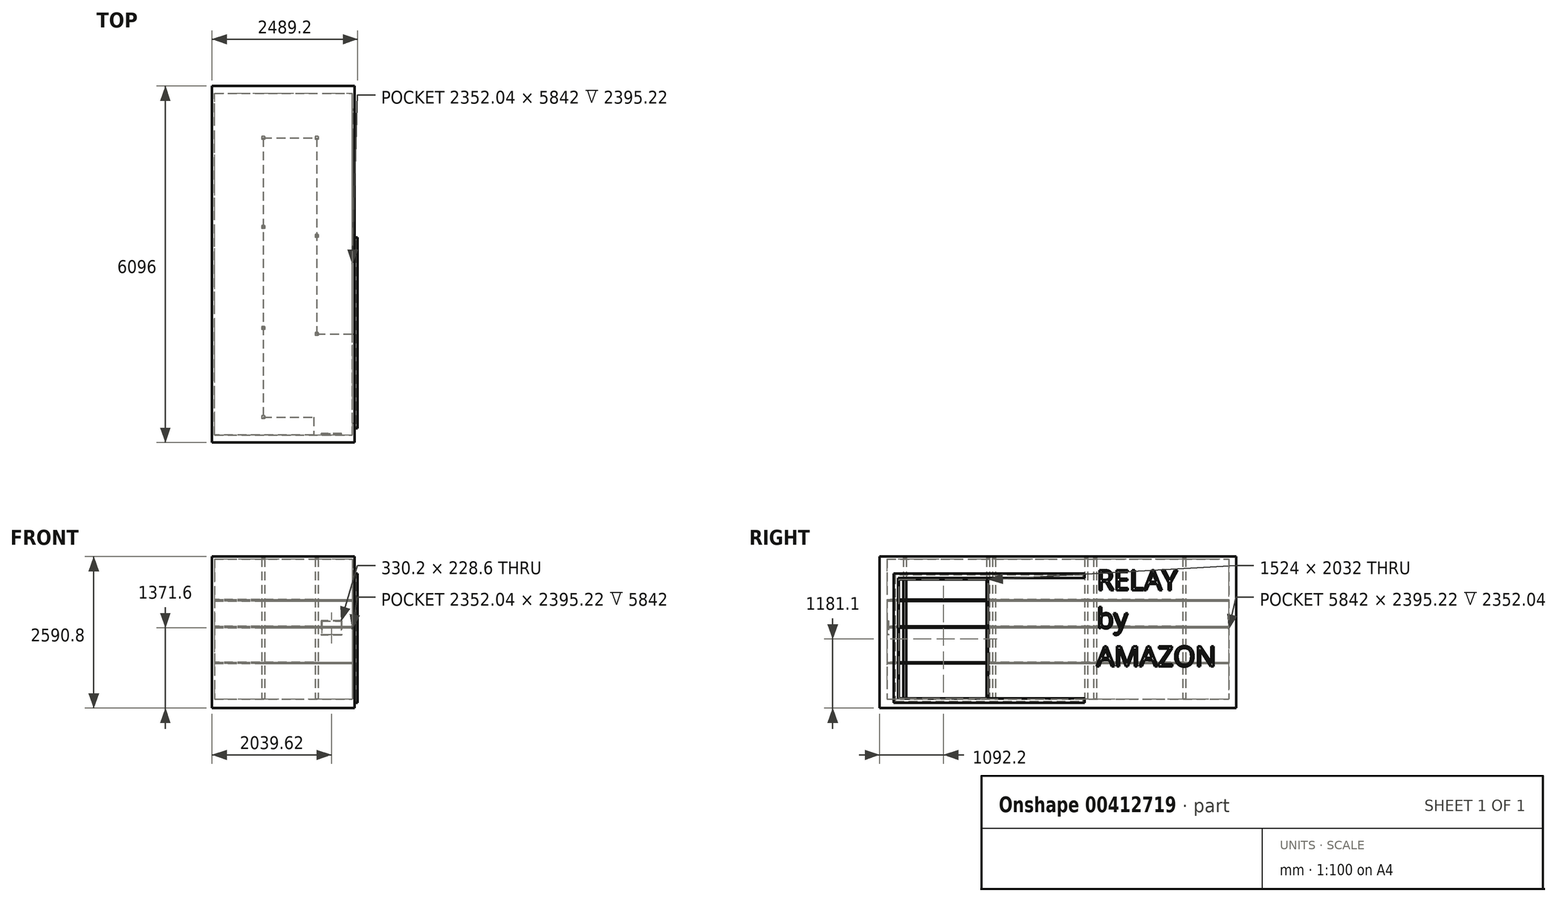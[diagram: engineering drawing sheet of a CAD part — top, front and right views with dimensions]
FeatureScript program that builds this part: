
annotation { "Feature Type Name" : "Feature", "Feature Type Description" : "" }
export const myFeature = defineFeature(function(context is Context, id is Id, definition is map)
    precondition{}
    {
        {
            var Q0;
            Q0=qCreatedBy(makeId("Front.planeOp"),FACE);
            var sketch = newSketch(context, id + "F0", { "sketchPlane" : qUnion([Q0])});
            skLineSegment(sketch, "E0.bottom", {"start": v(-1219.2, 1295.4) * mm, "end": v(1219.2, 1295.4) * mm});
            skLineSegment(sketch, "E0.top", {"start": v(-1219.2, -1295.4) * mm, "end": v(1219.2, -1295.4) * mm});
            skLineSegment(sketch, "E0.left", {"start": v(-1219.2, 1295.4) * mm, "end": v(-1219.2, -1295.4) * mm});
            skLineSegment(sketch, "E0.right", {"start": v(1219.2, 1295.4) * mm, "end": v(1219.2, -1295.4) * mm});
            skPoint(sketch, "E1", {"position": v(0, 1295.4) * mm});
            skPoint(sketch, "E2", {"position": v(-1219.2, 0) * mm});
            skLineSegment(sketch, "E3.bottom", {"start": v(-1176.02, 1252.22) * mm, "end": v(1176.02, 1252.22) * mm});
            skLineSegment(sketch, "E3.top", {"start": v(-1176.02, -1143) * mm, "end": v(1176.02, -1143) * mm});
            skLineSegment(sketch, "E3.left", {"start": v(-1176.02, 1252.22) * mm, "end": v(-1176.02, -1143) * mm});
            skLineSegment(sketch, "E3.right", {"start": v(1176.02, 1252.22) * mm, "end": v(1176.02, -1143) * mm});
            skPoint(sketch, "E4", {"position": v(0, 1252.22) * mm});
            skSolve(sketch);
        }
        {
            var Q0;
            Q0=makeQuery(id+"F0.imprint","IMPRINT",FACE,{"disambiguationData":[TD([[makeQuery(id+"F0.imprint","IMPRINT",EDGE,{"derivedFrom":sQuery(id+"F0.wireOp",EDGE,"E0.bottom")}),-1.0]])]});
            extrude(context, id + "F1", {"entities" : qUnion([Q0]), "depth" : 6096 * mm});
        }
        {
            var Q0;
            Q0=makeQuery(id+"F1.opExtrude","CAP_FACE",FACE,{"disambiguationData":[OSD([sQuery(id+"F0.wireOp",EDGE,"E0.bottom"),sQuery(id+"F0.wireOp",EDGE,"E0.top"),sQuery(id+"F0.wireOp",EDGE,"E0.left"),sQuery(id+"F0.wireOp",EDGE,"E0.right"),sQuery(id+"F0.wireOp",EDGE,"E3.bottom"),sQuery(id+"F0.wireOp",EDGE,"E3.top"),sQuery(id+"F0.wireOp",EDGE,"E3.left"),sQuery(id+"F0.wireOp",EDGE,"E3.right")])],"isStart":true});
            var sketch = newSketch(context, id + "F2", { "sketchPlane" : qUnion([Q0])});
            skLineSegment(sketch, "E5.0", {"start": v(1176.02, -1143) * mm, "end": v(-1176.02, -1143) * mm});
            skLineSegment(sketch, "E5.1", {"start": v(-1176.02, 1252.22) * mm, "end": v(-1176.02, -1143) * mm});
            skLineSegment(sketch, "E5.2", {"start": v(1176.02, 1252.22) * mm, "end": v(-1176.02, 1252.22) * mm});
            skLineSegment(sketch, "E5.3", {"start": v(1176.02, 1252.22) * mm, "end": v(1176.02, -1143) * mm});
            skSolve(sketch);
        }
        {
            var Q0;
            Q0 = qSketchRegion(id + "F2", true);
            extrude(context, id + "F3", {"entities" : qUnion([Q0]), "operationType" : NewBodyOperationType.ADD, "oppositeDirection" : true, "depth" : 127 * mm});
        }
        {
            var Q0;
            Q0=makeQuery(id+"F1.opExtrude","CAP_FACE",FACE,{"disambiguationData":[OSD([sQuery(id+"F0.wireOp",EDGE,"E0.bottom"),sQuery(id+"F0.wireOp",EDGE,"E0.top"),sQuery(id+"F0.wireOp",EDGE,"E0.left"),sQuery(id+"F0.wireOp",EDGE,"E0.right"),sQuery(id+"F0.wireOp",EDGE,"E3.bottom"),sQuery(id+"F0.wireOp",EDGE,"E3.top"),sQuery(id+"F0.wireOp",EDGE,"E3.left"),sQuery(id+"F0.wireOp",EDGE,"E3.right")])],"isStart":false});
            var sketch = newSketch(context, id + "F4", { "sketchPlane" : qUnion([Q0])});
            skLineSegment(sketch, "E6.0", {"start": v(-1176.02, -1143) * mm, "end": v(1176.02, -1143) * mm});
            skLineSegment(sketch, "E6.1", {"start": v(1176.02, 1252.22) * mm, "end": v(1176.02, -1143) * mm});
            skLineSegment(sketch, "E6.2", {"start": v(-1176.02, 1252.22) * mm, "end": v(1176.02, 1252.22) * mm});
            skLineSegment(sketch, "E6.3", {"start": v(-1176.02, 1252.22) * mm, "end": v(-1176.02, -1143) * mm});
            skSolve(sketch);
        }
        {
            var Q0;
            Q0 = qSketchRegion(id + "F4", true);
            extrude(context, id + "F5", {"entities" : qUnion([Q0]), "operationType" : NewBodyOperationType.ADD, "oppositeDirection" : true, "depth" : 127 * mm});
        }
        {
            var Q0;
            Q0=makeQuery(id+"F1.opExtrude","SWEPT_FACE",FACE,{"disambiguationData":[OSD([sQuery(id+"F0.wireOp",EDGE,"E0.right")])]});
            var sketch = newSketch(context, id + "F6", { "sketchPlane" : qUnion([Q0])});
            skLineSegment(sketch, "E7.bottom", {"start": v(-5765.8, 901.7) * mm, "end": v(-4241.8, 901.7) * mm});
            skLineSegment(sketch, "E7.top", {"start": v(-5765.8, -1130.3) * mm, "end": v(-4241.8, -1130.3) * mm});
            skLineSegment(sketch, "E7.left", {"start": v(-5765.8, 901.7) * mm, "end": v(-5765.8, -1130.3) * mm});
            skLineSegment(sketch, "E7.right", {"start": v(-4241.8, 901.7) * mm, "end": v(-4241.8, -1130.3) * mm});
            skSolve(sketch);
        }
        {
            var Q0;
            Q0 = qSketchRegion(id + "F6", true);
            extrude(context, id + "F7", {"entities" : qUnion([Q0]), "operationType" : NewBodyOperationType.REMOVE, "oppositeDirection" : true, "depth" : 50.8 * mm});
        }
        {
            var Q0;
            Q0=makeQuery(id+"F1.opExtrude","SWEPT_FACE",FACE,{"disambiguationData":[OSD([sQuery(id+"F0.wireOp",EDGE,"E0.right")])]});
            var sketch = newSketch(context, id + "F8", { "sketchPlane" : qUnion([Q0])});
            skLineSegment(sketch, "E8.left", {"start": v(-5778.5, -1130.3) * mm, "end": v(-5778.5, 927.1) * mm});
            skLineSegment(sketch, "E8.right", {"start": v(-5854.7, -1206.5) * mm, "end": v(-5854.7, 1003.3) * mm});
            skLineSegment(sketch, "E9.bottom", {"start": v(-5854.7, 1003.3) * mm, "end": v(-2590.8, 1003.3) * mm});
            skLineSegment(sketch, "E9.top", {"start": v(-5778.5, 927.1) * mm, "end": v(-2590.8, 927.1) * mm});
            skLineSegment(sketch, "E9.right", {"start": v(-2590.8, 1003.3) * mm, "end": v(-2590.8, 927.1) * mm});
            skLineSegment(sketch, "E10.bottom", {"start": v(-5778.5, -1130.3) * mm, "end": v(-2590.8, -1130.3) * mm});
            skLineSegment(sketch, "E10.top", {"start": v(-5854.7, -1206.5) * mm, "end": v(-2590.8, -1206.5) * mm});
            skLineSegment(sketch, "E10.right", {"start": v(-2590.8, -1130.3) * mm, "end": v(-2590.8, -1206.5) * mm});
            skSolve(sketch);
        }
        {
            var Q0;
            {var subQ0=sQuery(id+"F8.wireOp",EDGE,"E8.left");Q0=makeQuery(id+"F8.imprint","IMPRINT",FACE,{"disambiguationData":[TD([[makeQuery(id+"F8.imprint","IMPRINT",EDGE,{"derivedFrom":subQ0}),1.0]])]});}
            extrude(context, id + "F9", {"entities" : qUnion([Q0]), "operationType" : NewBodyOperationType.ADD, "depth" : 50.8 * mm});
        }
        {
            var Q0;
            Q0=makeQuery(id+"F1.opExtrude","SWEPT_FACE",FACE,{"disambiguationData":[OSD([sQuery(id+"F0.wireOp",EDGE,"E0.right")])]});
            var sketch = newSketch(context, id + "F10", { "sketchPlane" : qUnion([Q0])});
            skLineSegment(sketch, "E11.0", {"start": v(-5778.5, -1130.3) * mm, "end": v(-5778.5, 927.1) * mm});
            skLineSegment(sketch, "E12", {"start": v(-5778.5, 927.1) * mm, "end": v(-2616.2, 927.1) * mm});
            skLineSegment(sketch, "E13", {"start": v(-2616.2, 927.1) * mm, "end": v(-2616.2, 977.9) * mm});
            skLineSegment(sketch, "E14", {"start": v(-2616.2, 977.9) * mm, "end": v(-5829.3, 977.9) * mm});
            skLineSegment(sketch, "E15", {"start": v(-5829.3, 977.9) * mm, "end": v(-5829.3, -1181.1) * mm});
            skLineSegment(sketch, "E16", {"start": v(-5829.3, -1181.1) * mm, "end": v(-2616.2, -1181.1) * mm});
            skLineSegment(sketch, "E17", {"start": v(-2616.2, -1181.1) * mm, "end": v(-2616.2, -1130.3) * mm});
            skLineSegment(sketch, "E18", {"start": v(-2616.2, -1130.3) * mm, "end": v(-5778.5, -1130.3) * mm});
            skSolve(sketch);
        }
        {
            var Q0;
            Q0 = qSketchRegion(id + "F10", true);
            extrude(context, id + "F11", {"entities" : qUnion([Q0]), "operationType" : NewBodyOperationType.REMOVE, "depth" : 38.1 * mm});
        }
        {
            var Q0;
            Q0=makeQuery(id+"F11.boolean.opBoolean","MERGE",FACE,{"derivedFrom":[makeQuery(id+"F1.opExtrude","SWEPT_FACE",FACE,{"disambiguationData":[OSD([sQuery(id+"F0.wireOp",EDGE,"E0.right")])]}),makeQuery(id+"F11.opExtrude","CAP_FACE",FACE,{"disambiguationData":[OSD([sQuery(id+"F10.wireOp",EDGE,"E11.0"),sQuery(id+"F10.wireOp",EDGE,"E12"),sQuery(id+"F10.wireOp",EDGE,"E13"),sQuery(id+"F10.wireOp",EDGE,"E14"),sQuery(id+"F10.wireOp",EDGE,"E15"),sQuery(id+"F10.wireOp",EDGE,"E16"),sQuery(id+"F10.wireOp",EDGE,"E17"),sQuery(id+"F10.wireOp",EDGE,"E18")])],"isStart":true})]});
            var sketch = newSketch(context, id + "F12", { "sketchPlane" : qUnion([Q0])});
            skText(sketch, "E19", { "text": "RELAY\nby\nAMAZON", "fontName": "OpenSans-Regular.ttf"});
            const initialGuessF12  = {"E19": [-2.3876, 0.72163, 1, 0, 0.34517]};
            skSetInitialGuess(sketch, initialGuessF12);
            skSolve(sketch);
        }
        {
            var Q0;
            Q0 = qSketchRegion(id + "F12", true);
            extrude(context, id + "F13", {"entities" : qUnion([Q0]), "operationType" : NewBodyOperationType.REMOVE, "oppositeDirection" : true, "depth" : 12.7 * mm});
        }
        {
            var Q0;
            Q0=makeQuery(id+"F1.opExtrude","SWEPT_FACE",FACE,{"disambiguationData":[OSD([sQuery(id+"F0.wireOp",EDGE,"E3.top")])]});
            var sketch = newSketch(context, id + "F14", { "sketchPlane" : qUnion([Q0])});
            skLineSegment(sketch, "E20", {"start": v(-347.98, -889) * mm, "end": v(-347.98, -5664.2) * mm, "construction": true});
            skLineSegment(sketch, "E21", {"start": v(-347.98, -5664.2) * mm, "end": v(515.62, -5664.2) * mm, "construction": true});
            skLineSegment(sketch, "E22", {"start": v(515.62, -5664.2) * mm, "end": v(515.62, -5969) * mm, "construction": true});
            skLineSegment(sketch, "E23", {"start": v(-347.98, -889) * mm, "end": v(566.42, -889) * mm, "construction": true});
            skLineSegment(sketch, "E24", {"start": v(566.42, -889) * mm, "end": v(566.42, -4241.8) * mm, "construction": true});
            skLineSegment(sketch, "E25", {"start": v(566.42, -4241.8) * mm, "end": v(1176.02, -4241.8) * mm, "construction": true});
            skLineSegment(sketch, "E26.bottom", {"start": v(-322.58, -863.6) * mm, "end": v(-373.38, -863.6) * mm});
            skLineSegment(sketch, "E26.top", {"start": v(-322.58, -914.4) * mm, "end": v(-373.38, -914.4) * mm});
            skLineSegment(sketch, "E26.left", {"start": v(-322.58, -863.6) * mm, "end": v(-322.58, -914.4) * mm});
            skLineSegment(sketch, "E26.right", {"start": v(-373.38, -863.6) * mm, "end": v(-373.38, -914.4) * mm});
            skPoint(sketch, "E26.middle", {"position": v(-347.98, -889) * mm});
            skLineSegment(sketch, "E27.bottom", {"start": v(591.82, -863.6) * mm, "end": v(541.02, -863.6) * mm});
            skLineSegment(sketch, "E27.top", {"start": v(591.82, -914.4) * mm, "end": v(541.02, -914.4) * mm});
            skLineSegment(sketch, "E27.left", {"start": v(591.82, -863.6) * mm, "end": v(591.82, -914.4) * mm});
            skLineSegment(sketch, "E27.right", {"start": v(541.02, -863.6) * mm, "end": v(541.02, -914.4) * mm});
            skPoint(sketch, "E27.middle", {"position": v(566.42, -889) * mm});
            skLineSegment(sketch, "E28.bottom", {"start": v(-322.58, -5638.8) * mm, "end": v(-373.38, -5638.8) * mm});
            skLineSegment(sketch, "E28.top", {"start": v(-322.58, -5689.6) * mm, "end": v(-373.38, -5689.6) * mm});
            skLineSegment(sketch, "E28.left", {"start": v(-322.58, -5638.8) * mm, "end": v(-322.58, -5689.6) * mm});
            skLineSegment(sketch, "E28.right", {"start": v(-373.38, -5638.8) * mm, "end": v(-373.38, -5689.6) * mm});
            skPoint(sketch, "E28.middle", {"position": v(-347.98, -5664.2) * mm});
            skPoint(sketch, "E29.middle", {"position": v(566.42, -4241.8) * mm});
            skLineSegment(sketch, "E30.bottom", {"start": v(-322.58, -2387.6) * mm, "end": v(-373.38, -2387.6) * mm});
            skLineSegment(sketch, "E30.top", {"start": v(-322.58, -2438.4) * mm, "end": v(-373.38, -2438.4) * mm});
            skLineSegment(sketch, "E30.left", {"start": v(-322.58, -2387.6) * mm, "end": v(-322.58, -2438.4) * mm});
            skLineSegment(sketch, "E30.right", {"start": v(-373.38, -2387.6) * mm, "end": v(-373.38, -2438.4) * mm});
            skPoint(sketch, "E30.middle", {"position": v(-347.98, -2413) * mm});
            skLineSegment(sketch, "E31.bottom", {"start": v(-322.58, -4114.8) * mm, "end": v(-373.38, -4114.8) * mm});
            skLineSegment(sketch, "E31.top", {"start": v(-322.58, -4165.6) * mm, "end": v(-373.38, -4165.6) * mm});
            skLineSegment(sketch, "E31.left", {"start": v(-322.58, -4114.8) * mm, "end": v(-322.58, -4165.6) * mm});
            skLineSegment(sketch, "E31.right", {"start": v(-373.38, -4114.8) * mm, "end": v(-373.38, -4165.6) * mm});
            skPoint(sketch, "E31.middle", {"position": v(-347.98, -4140.2) * mm});
            skLineSegment(sketch, "E32.bottom", {"start": v(591.82, -2540) * mm, "end": v(541.02, -2540) * mm});
            skLineSegment(sketch, "E32.top", {"start": v(591.82, -2590.8) * mm, "end": v(541.02, -2590.8) * mm});
            skLineSegment(sketch, "E32.left", {"start": v(591.82, -2540) * mm, "end": v(591.82, -2590.8) * mm});
            skLineSegment(sketch, "E32.right", {"start": v(541.02, -2540) * mm, "end": v(541.02, -2590.8) * mm});
            skPoint(sketch, "E32.middle", {"position": v(566.42, -2565.4) * mm});
            skLineSegment(sketch, "E33.bottom", {"start": v(591.82, -4216.4) * mm, "end": v(541.02, -4216.4) * mm});
            skLineSegment(sketch, "E33.top", {"start": v(591.82, -4267.2) * mm, "end": v(541.02, -4267.2) * mm});
            skLineSegment(sketch, "E33.left", {"start": v(591.82, -4216.4) * mm, "end": v(591.82, -4267.2) * mm});
            skLineSegment(sketch, "E33.right", {"start": v(541.02, -4216.4) * mm, "end": v(541.02, -4267.2) * mm});
            skSolve(sketch);
        }
        {
            var Q0;
            Q0 = qSketchRegion(id + "F14", true);
            extrude(context, id + "F15", {"entities" : qUnion([Q0]), "depth" : 2413 * mm});
        }
        {
            var Q0;
            Q0=makeQuery(id+"F14.imprint","IMPRINT",FACE,{"disambiguationData":[TD([[makeQuery(id+"F14.imprint","IMPRINT",EDGE,{"derivedFrom":sQuery(id+"F14.wireOp",EDGE,"E26.bottom")}),-1.0]])]});
            cPlane(context, id + "F16", {"entities" : qUnion([Q0]), "cplaneType" : CPlaneType.OFFSET, "offset" : 609.6 * mm, "width" : 152.4 * mm, "height" : 152.4 * mm});
        }
        {
            var Q0;
            Q0=qCreatedBy(id+"F16.planeOp",FACE);
            var sketch = newSketch(context, id + "F17", { "sketchPlane" : qUnion([Q0])});
            skLineSegment(sketch, "E34.0", {"start": v(566.42, -4241.8) * mm, "end": v(1176.02, -4241.8) * mm});
            skLineSegment(sketch, "E34.1", {"start": v(566.42, -889) * mm, "end": v(566.42, -4241.8) * mm});
            skLineSegment(sketch, "E34.2", {"start": v(-347.98, -889) * mm, "end": v(566.42, -889) * mm});
            skLineSegment(sketch, "E34.3", {"start": v(-347.98, -889) * mm, "end": v(-347.98, -5664.2) * mm});
            skLineSegment(sketch, "E34.4", {"start": v(-347.98, -5664.2) * mm, "end": v(515.62, -5664.2) * mm});
            skLineSegment(sketch, "E34.5", {"start": v(515.62, -5664.2) * mm, "end": v(515.62, -5969) * mm});
            skLineSegment(sketch, "E35", {"start": v(515.62, -5969) * mm, "end": v(-1176.02, -5969) * mm});
            skLineSegment(sketch, "E36", {"start": v(-1176.02, -5969) * mm, "end": v(-1176.02, -127) * mm});
            skLineSegment(sketch, "E37.0", {"start": v(-1176.02, -127) * mm, "end": v(1176.02, -127) * mm});
            skLineSegment(sketch, "E38.0", {"start": v(1176.02, -4241.8) * mm, "end": v(1176.02, -127) * mm});
            skPoint(sketch, "E39.orphan", {"position": v(1176.02, -5969) * mm});
            skSolve(sketch);
        }
        {
            var Q0;
            Q0 = qSketchRegion(id + "F17", true);
            extrude(context, id + "F18", {"entities" : qUnion([Q0]), "depth" : 19.05 * mm});
        }
        {
            var Q0;
            Q0=qCreatedBy(id+"F16.planeOp",FACE);
            cPlane(context, id + "F19", {"entities" : qUnion([Q0]), "cplaneType" : CPlaneType.OFFSET, "offset" : 609.6 * mm, "width" : 152.4 * mm, "height" : 152.4 * mm});
        }
        {
            var Q0;
            Q0=qCreatedBy(id+"F19.planeOp",FACE);
            var sketch = newSketch(context, id + "F20", { "sketchPlane" : qUnion([Q0])});
            skLineSegment(sketch, "E40.0", {"start": v(566.42, -4241.8) * mm, "end": v(1176.02, -4241.8) * mm});
            skLineSegment(sketch, "E40.1", {"start": v(566.42, -889) * mm, "end": v(566.42, -4241.8) * mm});
            skLineSegment(sketch, "E40.2", {"start": v(-347.98, -889) * mm, "end": v(566.42, -889) * mm});
            skLineSegment(sketch, "E40.3", {"start": v(-347.98, -889) * mm, "end": v(-347.98, -5664.2) * mm});
            skLineSegment(sketch, "E40.4", {"start": v(-347.98, -5664.2) * mm, "end": v(515.62, -5664.2) * mm});
            skLineSegment(sketch, "E40.5", {"start": v(515.62, -5664.2) * mm, "end": v(515.62, -5969) * mm});
            skLineSegment(sketch, "E40.6", {"start": v(515.62, -5969) * mm, "end": v(-1176.02, -5969) * mm});
            skLineSegment(sketch, "E40.7", {"start": v(-1176.02, -5969) * mm, "end": v(-1176.02, -127) * mm});
            skLineSegment(sketch, "E40.8", {"start": v(-1176.02, -127) * mm, "end": v(1176.02, -127) * mm});
            skLineSegment(sketch, "E40.9", {"start": v(1176.02, -4241.8) * mm, "end": v(1176.02, -127) * mm});
            skPoint(sketch, "E40.10", {"position": v(1176.02, -5969) * mm});
            skSolve(sketch);
        }
        {
            var Q0;
            Q0=qCreatedBy(id+"F19.planeOp",FACE);
            cPlane(context, id + "F21", {"entities" : qUnion([Q0]), "cplaneType" : CPlaneType.OFFSET, "offset" : 457.2 * mm, "width" : 152.4 * mm, "height" : 152.4 * mm});
        }
        {
            var Q0;
            Q0=qCreatedBy(id+"F21.planeOp",FACE);
            var sketch = newSketch(context, id + "F22", { "sketchPlane" : qUnion([Q0])});
            skLineSegment(sketch, "E41.0", {"start": v(566.42, -4241.8) * mm, "end": v(1176.02, -4241.8) * mm});
            skLineSegment(sketch, "E41.1", {"start": v(566.42, -889) * mm, "end": v(566.42, -4241.8) * mm});
            skLineSegment(sketch, "E41.2", {"start": v(-347.98, -889) * mm, "end": v(566.42, -889) * mm});
            skLineSegment(sketch, "E41.3", {"start": v(-347.98, -889) * mm, "end": v(-347.98, -5664.2) * mm});
            skLineSegment(sketch, "E41.4", {"start": v(-347.98, -5664.2) * mm, "end": v(515.62, -5664.2) * mm});
            skLineSegment(sketch, "E41.5", {"start": v(515.62, -5664.2) * mm, "end": v(515.62, -5969) * mm});
            skLineSegment(sketch, "E41.6", {"start": v(515.62, -5969) * mm, "end": v(-1176.02, -5969) * mm});
            skLineSegment(sketch, "E41.7", {"start": v(-1176.02, -5969) * mm, "end": v(-1176.02, -127) * mm});
            skLineSegment(sketch, "E41.8", {"start": v(-1176.02, -127) * mm, "end": v(1176.02, -127) * mm});
            skLineSegment(sketch, "E41.9", {"start": v(1176.02, -4241.8) * mm, "end": v(1176.02, -127) * mm});
            skPoint(sketch, "E41.10", {"position": v(1176.02, -5969) * mm});
            skSolve(sketch);
        }
        {
            var Q0;
            Q0 = qSketchRegion(id + "F20", true);
            extrude(context, id + "F23", {"entities" : qUnion([Q0]), "depth" : 25.4 * mm});
        }
        {
            var Q0;
            Q0 = qSketchRegion(id + "F22", true);
            extrude(context, id + "F24", {"entities" : qUnion([Q0]), "depth" : 25.4 * mm});
        }
        {
            var Q0;
            Q0=makeQuery(id+"F5.opExtrude","CAP_FACE",FACE,{"disambiguationData":[OSD([sQuery(id+"F4.wireOp",EDGE,"E6.0"),sQuery(id+"F4.wireOp",EDGE,"E6.1"),sQuery(id+"F4.wireOp",EDGE,"E6.2"),sQuery(id+"F4.wireOp",EDGE,"E6.3")])],"isStart":false});
            var sketch = newSketch(context, id + "F25", { "sketchPlane" : qUnion([Q0])});
            skLineSegment(sketch, "E42.bottom", {"start": v(-655.32, 190.5) * mm, "end": v(-985.52, 190.5) * mm});
            skLineSegment(sketch, "E42.top", {"start": v(-655.32, -38.1) * mm, "end": v(-985.52, -38.1) * mm});
            skLineSegment(sketch, "E42.left", {"start": v(-655.32, 190.5) * mm, "end": v(-655.32, -38.1) * mm});
            skLineSegment(sketch, "E42.right", {"start": v(-985.52, 190.5) * mm, "end": v(-985.52, -38.1) * mm});
            skPoint(sketch, "E42.middle", {"position": v(-820.42, 76.2) * mm});
            skSolve(sketch);
        }
        {
            var Q0;
            Q0=makeQuery(id+"F25.imprint","IMPRINT",FACE,{"disambiguationData":[TD([[makeQuery(id+"F25.imprint","IMPRINT",EDGE,{"derivedFrom":sQuery(id+"F25.wireOp",EDGE,"E42.bottom")}),1.0]])]});
            extrude(context, id + "F26", {"entities" : qUnion([Q0]), "depth" : 25.4 * mm});
        }
        {
            var Q0;
            Q0=makeQuery(id+"F26.opExtrude","CAP_FACE",FACE,{"disambiguationData":[OSD([sQuery(id+"F25.wireOp",EDGE,"E42.bottom"),sQuery(id+"F25.wireOp",EDGE,"E42.top"),sQuery(id+"F25.wireOp",EDGE,"E42.left"),sQuery(id+"F25.wireOp",EDGE,"E42.right")])],"isStart":false});
            var sketch = newSketch(context, id + "F27", { "sketchPlane" : qUnion([Q0])});
            skLineSegment(sketch, "E43.bottom", {"start": v(-985.52, 190.5) * mm, "end": v(-655.32, 190.5) * mm});
            skLineSegment(sketch, "E43.top", {"start": v(-985.52, -38.1) * mm, "end": v(-655.32, -38.1) * mm});
            skLineSegment(sketch, "E43.left", {"start": v(-985.52, 190.5) * mm, "end": v(-985.52, -38.1) * mm});
            skLineSegment(sketch, "E43.right", {"start": v(-655.32, 190.5) * mm, "end": v(-655.32, -38.1) * mm});
            skLineSegment(sketch, "E44.0", {"start": v(-996.95, 201.93) * mm, "end": v(-643.89, 201.93) * mm});
            skLineSegment(sketch, "E44.1", {"start": v(-996.95, 201.93) * mm, "end": v(-996.95, -49.53) * mm});
            skLineSegment(sketch, "E44.2", {"start": v(-996.95, -49.53) * mm, "end": v(-643.89, -49.53) * mm});
            skLineSegment(sketch, "E44.3", {"start": v(-643.89, 201.93) * mm, "end": v(-643.89, -49.53) * mm});
            skSolve(sketch);
        }
        {
            var Q0;
            Q0 = qSketchRegion(id + "F27", true);
            extrude(context, id + "F28", {"entities" : qUnion([Q0]), "oppositeDirection" : true, "depth" : 2.54 * mm});
        }
    });
